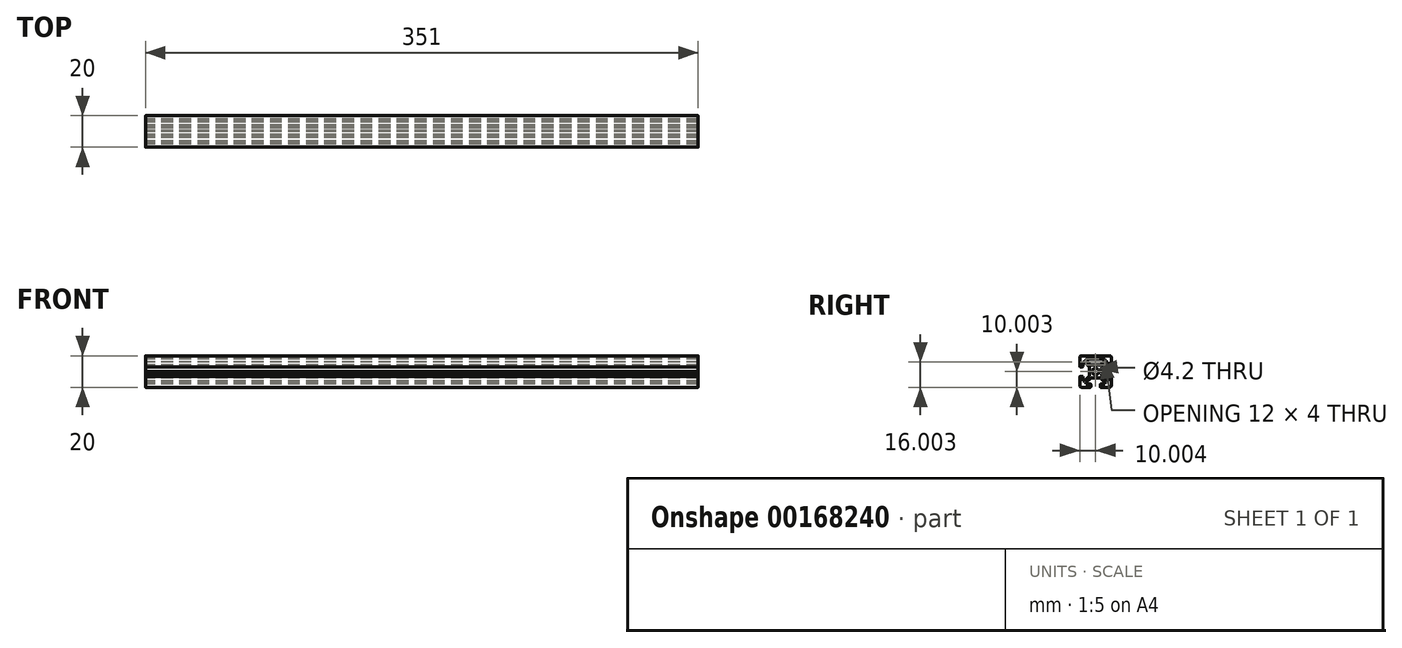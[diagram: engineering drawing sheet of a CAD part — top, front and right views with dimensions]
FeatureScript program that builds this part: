
annotation { "Feature Type Name" : "Feature", "Feature Type Description" : "" }
export const myFeature = defineFeature(function(context is Context, id is Id, definition is map)
    precondition{}
    {
        {
            var Q0;
            Q0=qCreatedBy(makeId("Right.planeOp"),FACE);
            var sketch = newSketch(context, id + "F0", { "sketchPlane" : qUnion([Q0])});
            skLineSegment(sketch, "E0", {"start": v(0.04, 10.07) * mm, "end": v(-8.96, 10.07) * mm});
            skLineSegment(sketch, "E1", {"start": v(-9.96, 9.07) * mm, "end": v(-9.96, 3.37) * mm});
            skLineSegment(sketch, "E2", {"start": v(-3.96, 3.01) * mm, "end": v(-3.96, 0.73) * mm});
            skLineSegment(sketch, "E3", {"start": v(0.04, 4.07) * mm, "end": v(-2.69, 4.07) * mm});
            skLineSegment(sketch, "E4", {"start": v(0.04, 8.07) * mm, "end": v(-5.46, 8.07) * mm});
            skLineSegment(sketch, "E5", {"start": v(-7.96, 6.07) * mm, "end": v(-7.96, 3.37) * mm});
            skLineSegment(sketch, "E6", {"start": v(-8.26, 3.07) * mm, "end": v(-9.66, 3.07) * mm});
            skLineSegment(sketch, "E7", {"start": v(-8.26, -2.93) * mm, "end": v(-9.66, -2.93) * mm});
            skLineSegment(sketch, "E8", {"start": v(-7.02, -5.93) * mm, "end": v(-7.96, -5.93) * mm});
            skLineSegment(sketch, "E9", {"start": v(-7.96, -3.23) * mm, "end": v(-7.96, -5.93) * mm});
            skLineSegment(sketch, "E10", {"start": v(-9.96, -3.23) * mm, "end": v(-9.96, -8.93) * mm});
            skLineSegment(sketch, "E11", {"start": v(-7.02, 6.07) * mm, "end": v(-7.96, 6.07) * mm});
            skLineSegment(sketch, "E12", {"start": v(-3.89, -0.33) * mm, "end": v(-3.66, 0.07) * mm});
            skLineSegment(sketch, "E13", {"start": v(-3.89, 0.48) * mm, "end": v(-3.66, 0.07) * mm});
            skLineSegment(sketch, "E14", {"start": v(-3.96, -2.43) * mm, "end": v(-3.96, -2.87) * mm});
            skLineSegment(sketch, "E15", {"start": v(-3.96, 3.01) * mm, "end": v(-7.02, 6.07) * mm});
            skLineSegment(sketch, "E16", {"start": v(-3.96, -2.87) * mm, "end": v(-7.02, -5.93) * mm});
            skLineSegment(sketch, "E17", {"start": v(-3.96, -2.43) * mm, "end": v(-3.7, -1.15) * mm});
            skArc(sketch, "E18", {"start": v(-3.89, -0.33) * mm, "mid": v(-3.96, -0.58) * mm, "end": v(-3.89, -0.83) * mm});
            skLineSegment(sketch, "E19", {"start": v(-3.89, -0.83) * mm, "end": v(-3.7, -1.15) * mm});
            skArc(sketch, "E20", {"start": v(-3.96, 0.73) * mm, "mid": v(-3.94, 0.6) * mm, "end": v(-3.89, 0.48) * mm});
            skArc(sketch, "E21", {"start": v(-8.26, 3.07) * mm, "mid": v(-8.04, 3.16) * mm, "end": v(-7.96, 3.37) * mm});
            skArc(sketch, "E22", {"start": v(-9.96, 3.37) * mm, "mid": v(-9.87, 3.16) * mm, "end": v(-9.66, 3.07) * mm});
            skArc(sketch, "E23", {"start": v(-7.96, -3.23) * mm, "mid": v(-8.04, -3.01) * mm, "end": v(-8.26, -2.93) * mm});
            skArc(sketch, "E24", {"start": v(-9.66, -2.93) * mm, "mid": v(-9.87, -3.01) * mm, "end": v(-9.96, -3.23) * mm});
            skLineSegment(sketch, "E25", {"start": v(-2.9, -3.93) * mm, "end": v(-0.61, -3.93) * mm});
            skArc(sketch, "E26", {"start": v(-3.26, -9.93) * mm, "mid": v(-3.04, -9.84) * mm, "end": v(-2.96, -9.63) * mm});
            skLineSegment(sketch, "E27", {"start": v(-5.96, -7.93) * mm, "end": v(-3.26, -7.93) * mm});
            skArc(sketch, "E28", {"start": v(-2.96, -8.23) * mm, "mid": v(-3.04, -8.01) * mm, "end": v(-3.26, -7.93) * mm});
            skLineSegment(sketch, "E29", {"start": v(-5.96, -6.99) * mm, "end": v(-5.96, -7.93) * mm});
            skLineSegment(sketch, "E30", {"start": v(-2.96, -8.23) * mm, "end": v(-2.96, -9.63) * mm});
            skLineSegment(sketch, "E31", {"start": v(-0.36, -3.86) * mm, "end": v(-0.06, -3.69) * mm});
            skArc(sketch, "E32", {"start": v(-0.61, -3.93) * mm, "mid": v(-0.48, -3.9) * mm, "end": v(-0.36, -3.86) * mm});
            skLineSegment(sketch, "E33", {"start": v(-2.9, -3.93) * mm, "end": v(-5.96, -6.99) * mm});
            skLineSegment(sketch, "E34", {"start": v(-3.26, -9.93) * mm, "end": v(-8.96, -9.93) * mm});
            skLineSegment(sketch, "E35", {"start": v(-3.04, 4.22) * mm, "end": v(-5.8, 6.99) * mm});
            skLineSegment(sketch, "E36", {"start": v(-5.96, 7.57) * mm, "end": v(-5.96, 7.34) * mm});
            skArc(sketch, "E37", {"start": v(0.04, -2.03) * mm, "mid": v(-2.06, 0.07) * mm, "end": v(0.04, 2.17) * mm});
            skArc(sketch, "E38", {"start": v(-9.96, -8.93) * mm, "mid": v(-9.66, -9.63) * mm, "end": v(-8.96, -9.93) * mm});
            skArc(sketch, "E39", {"start": v(-8.96, 10.07) * mm, "mid": v(-9.66, 9.78) * mm, "end": v(-9.96, 9.07) * mm});
            skArc(sketch, "E40", {"start": v(-5.46, 8.07) * mm, "mid": v(-5.8, 7.93) * mm, "end": v(-5.96, 7.57) * mm});
            skArc(sketch, "E41", {"start": v(-5.96, 7.34) * mm, "mid": v(-5.92, 7.15) * mm, "end": v(-5.8, 6.99) * mm});
            skArc(sketch, "E42", {"start": v(-3.04, 4.22) * mm, "mid": v(-2.88, 4.11) * mm, "end": v(-2.69, 4.07) * mm});
            skArc(sketch, "E43.MirrorCS", {"start": v(8.34, 3.07) * mm, "mid": v(8.13, 3.16) * mm, "end": v(8.04, 3.37) * mm});
            skArc(sketch, "E44.MirrorCS", {"start": v(5.54, 8.07) * mm, "mid": v(5.9, 7.93) * mm, "end": v(6.04, 7.57) * mm});
            skLineSegment(sketch, "E45.MirrorCS", {"start": v(3.98, -0.33) * mm, "end": v(3.74, 0.07) * mm});
            skArc(sketch, "E46.MirrorCS", {"start": v(3.04, -8.23) * mm, "mid": v(3.13, -8.01) * mm, "end": v(3.34, -7.93) * mm});
            skLineSegment(sketch, "E47.MirrorCS", {"start": v(3.98, -0.83) * mm, "end": v(3.8, -1.15) * mm});
            skArc(sketch, "E48.MirrorCS", {"start": v(3.34, -9.93) * mm, "mid": v(3.13, -9.84) * mm, "end": v(3.04, -9.63) * mm});
            skLineSegment(sketch, "E49.MirrorCS", {"start": v(7.1, -5.93) * mm, "end": v(8.04, -5.93) * mm});
            skArc(sketch, "E50.MirrorCS", {"start": v(3.98, -0.33) * mm, "mid": v(4.04, -0.58) * mm, "end": v(3.98, -0.83) * mm});
            skLineSegment(sketch, "E51.MirrorCS", {"start": v(4.04, -2.43) * mm, "end": v(3.8, -1.15) * mm});
            skArc(sketch, "E52.MirrorCS", {"start": v(9.74, -2.93) * mm, "mid": v(9.96, -3.01) * mm, "end": v(10.04, -3.23) * mm});
            skArc(sketch, "E53.MirrorCS", {"start": v(0.7, -3.93) * mm, "mid": v(0.63, -3.92) * mm, "end": v(0.57, -3.91) * mm});
            skLineSegment(sketch, "E54.MirrorCS", {"start": v(6.04, 7.57) * mm, "end": v(6.04, 7.34) * mm});
            skLineSegment(sketch, "E55.MirrorCS", {"start": v(6.04, -6.99) * mm, "end": v(6.04, -7.93) * mm});
            skArc(sketch, "E56.MirrorCS", {"start": v(6.04, 7.34) * mm, "mid": v(6, 7.15) * mm, "end": v(5.9, 6.99) * mm});
            skArc(sketch, "E57.MirrorCS", {"start": v(4.04, 0.73) * mm, "mid": v(4.03, 0.6) * mm, "end": v(3.98, 0.48) * mm});
            skArc(sketch, "E58.MirrorCS", {"start": v(8.04, -3.23) * mm, "mid": v(8.13, -3.01) * mm, "end": v(8.34, -2.93) * mm});
            skArc(sketch, "E59.MirrorCS", {"start": v(10.04, 3.37) * mm, "mid": v(9.96, 3.16) * mm, "end": v(9.74, 3.07) * mm});
            skArc(sketch, "E60.MirrorCS", {"start": v(3.13, 4.22) * mm, "mid": v(2.97, 4.11) * mm, "end": v(2.78, 4.07) * mm});
            skLineSegment(sketch, "E61.MirrorCS", {"start": v(7.1, 6.07) * mm, "end": v(8.04, 6.07) * mm});
            skLineSegment(sketch, "E62.MirrorCS", {"start": v(4.04, -2.43) * mm, "end": v(4.04, -2.87) * mm});
            skLineSegment(sketch, "E63.MirrorCS", {"start": v(3.98, 0.48) * mm, "end": v(3.74, 0.07) * mm});
            skLineSegment(sketch, "E64.MirrorCS", {"start": v(3.04, -8.23) * mm, "end": v(3.04, -9.63) * mm});
            skLineSegment(sketch, "E65.MirrorCS", {"start": v(3.13, 4.22) * mm, "end": v(5.9, 6.99) * mm});
            skLineSegment(sketch, "E66.MirrorCS", {"start": v(10.04, -3.23) * mm, "end": v(10.04, -8.93) * mm});
            skLineSegment(sketch, "E67.MirrorCS", {"start": v(8.04, -3.23) * mm, "end": v(8.04, -5.93) * mm});
            skLineSegment(sketch, "E68.MirrorCS", {"start": v(8.34, -2.93) * mm, "end": v(9.74, -2.93) * mm});
            skLineSegment(sketch, "E69.MirrorCS", {"start": v(8.34, 3.07) * mm, "end": v(9.74, 3.07) * mm});
            skLineSegment(sketch, "E70.MirrorCS", {"start": v(2.98, -3.93) * mm, "end": v(0.7, -3.93) * mm});
            skLineSegment(sketch, "E71.MirrorCS", {"start": v(4.04, 3.01) * mm, "end": v(4.04, 0.73) * mm});
            skLineSegment(sketch, "E72.MirrorCS", {"start": v(4.04, -2.87) * mm, "end": v(7.1, -5.93) * mm});
            skLineSegment(sketch, "E73.MirrorCS", {"start": v(2.98, -3.93) * mm, "end": v(6.04, -6.99) * mm});
            skArc(sketch, "E74.MirrorCS", {"start": v(9.04, 10.07) * mm, "mid": v(9.75, 9.78) * mm, "end": v(10.04, 9.07) * mm});
            skLineSegment(sketch, "E75.MirrorCS", {"start": v(6.04, -7.93) * mm, "end": v(3.34, -7.93) * mm});
            skLineSegment(sketch, "E76.MirrorCS", {"start": v(4.04, 3.01) * mm, "end": v(7.1, 6.07) * mm});
            skArc(sketch, "E77.MirrorCS", {"start": v(10.04, -8.93) * mm, "mid": v(9.75, -9.63) * mm, "end": v(9.04, -9.93) * mm});
            skLineSegment(sketch, "E78.MirrorCS", {"start": v(3.34, -9.93) * mm, "end": v(9.04, -9.93) * mm});
            skLineSegment(sketch, "E79.MirrorCS", {"start": v(8.04, 6.07) * mm, "end": v(8.04, 3.37) * mm});
            skLineSegment(sketch, "E80.MirrorCS", {"start": v(10.04, 9.07) * mm, "end": v(10.04, 3.37) * mm});
            skLineSegment(sketch, "E81.MirrorCS", {"start": v(0.04, 10.07) * mm, "end": v(9.04, 10.07) * mm});
            skLineSegment(sketch, "E82.MirrorCS", {"start": v(0.04, 8.07) * mm, "end": v(5.54, 8.07) * mm});
            skLineSegment(sketch, "E83.MirrorCS", {"start": v(0.04, 4.07) * mm, "end": v(2.78, 4.07) * mm});
            skArc(sketch, "E84.MirrorCS", {"start": v(0.04, -2.03) * mm, "mid": v(2.14, 0.07) * mm, "end": v(0.04, 2.17) * mm});
            skLineSegment(sketch, "E85", {"start": v(0.22, -3.85) * mm, "end": v(-0.06, -3.69) * mm});
            skArc(sketch, "E86", {"start": v(0.22, -3.85) * mm, "mid": v(0.4, -3.92) * mm, "end": v(0.57, -3.91) * mm});
            skSolve(sketch);
        }
        {
            var Q0;
            Q0=qSketchRegion(id+"F0",true);
            extrude(context, id + "F1", {"entities" : qUnion([Q0]), "endBound" : BoundingType.SYMMETRIC, "depth" : 351 * mm});
        }
    });
